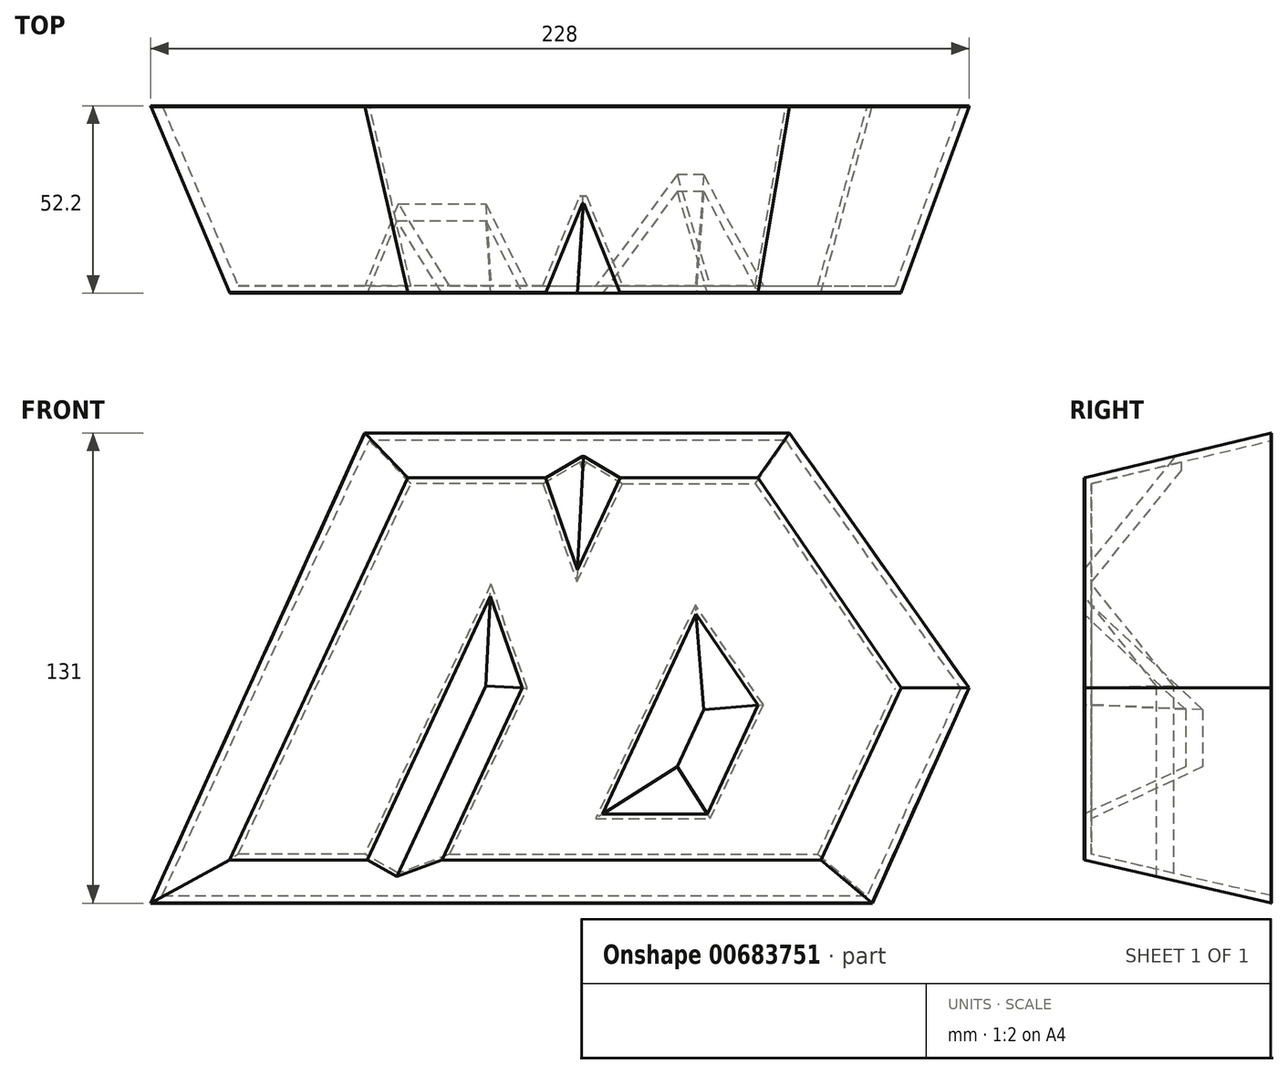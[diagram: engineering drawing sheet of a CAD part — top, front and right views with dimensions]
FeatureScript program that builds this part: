
annotation { "Feature Type Name" : "Feature", "Feature Type Description" : "" }
export const myFeature = defineFeature(function(context is Context, id is Id, definition is map)
    precondition{}
    {
        {
            var Q0;
            Q0=qCreatedBy(makeId("Front.planeOp"),FACE);
            var sketch = newSketch(context, id + "F0", { "sketchPlane" : qUnion([Q0])});
            skLineSegment(sketch, "E0", {"start": v(0, 0) * mm, "end": v(38.4, 0) * mm});
            skLineSegment(sketch, "E1", {"start": v(38.4, 0) * mm, "end": v(72.72, 73.6) * mm});
            skLineSegment(sketch, "E2", {"start": v(72.72, 73.6) * mm, "end": v(81.58, 48) * mm});
            skLineSegment(sketch, "E3", {"start": v(81.58, 48) * mm, "end": v(59.2, 0) * mm});
            skLineSegment(sketch, "E4", {"start": v(59.2, 0) * mm, "end": v(164.8, 0) * mm});
            skLineSegment(sketch, "E5", {"start": v(164.8, 0) * mm, "end": v(187.18, 48) * mm});
            skLineSegment(sketch, "E6", {"start": v(187.18, 48) * mm, "end": v(147.29, 106.56) * mm});
            skLineSegment(sketch, "E7", {"start": v(147.29, 106.56) * mm, "end": v(108.89, 106.56) * mm});
            skLineSegment(sketch, "E8", {"start": v(108.89, 106.56) * mm, "end": v(96.95, 80.96) * mm});
            skLineSegment(sketch, "E9", {"start": v(96.95, 80.96) * mm, "end": v(88.09, 106.56) * mm});
            skLineSegment(sketch, "E10", {"start": v(88.09, 106.56) * mm, "end": v(49.69, 106.56) * mm});
            skLineSegment(sketch, "E11", {"start": v(49.69, 106.56) * mm, "end": v(0, 0) * mm});
            skLineSegment(sketch, "E12", {"start": v(104, 12.8) * mm, "end": v(133.12, 12.8) * mm});
            skLineSegment(sketch, "E13", {"start": v(133.12, 12.8) * mm, "end": v(147.29, 43.19) * mm});
            skLineSegment(sketch, "E14", {"start": v(147.29, 43.19) * mm, "end": v(130, 68.56) * mm});
            skLineSegment(sketch, "E15", {"start": v(130, 68.56) * mm, "end": v(104, 12.8) * mm});
            skLineSegment(sketch, "E16", {"start": v(38.4, 0) * mm, "end": v(59.2, 0) * mm});
            skLineSegment(sketch, "E17", {"start": v(88.09, 106.56) * mm, "end": v(108.89, 106.56) * mm});
            skSolve(sketch);
        }
        {
            var Q0;
            Q0=qCreatedBy(makeId("Front.planeOp"),FACE);
            cPlane(context, id + "F1", {"entities" : qUnion([Q0]), "cplaneType" : CPlaneType.OFFSET, "offset" : 52 * mm, "oppositeDirection" : true, "width" : 150 * mm, "height" : 150 * mm});
        }
        {
            var Q0;
            Q0=qCreatedBy(id+"F1.planeOp",FACE);
            var sketch = newSketch(context, id + "F2", { "sketchPlane" : qUnion([Q0])});
            skLineSegment(sketch, "E18", {"start": v(179.07, -12) * mm, "end": v(206.07, 48) * mm});
            skLineSegment(sketch, "E19", {"start": v(206.07, 48) * mm, "end": v(156.07, 119) * mm});
            skLineSegment(sketch, "E20", {"start": v(37.7, 119) * mm, "end": v(-21.93, -12) * mm});
            skLineSegment(sketch, "E21", {"start": v(-21.93, -12) * mm, "end": v(179.07, -12) * mm});
            skLineSegment(sketch, "E22", {"start": v(37.69, 119) * mm, "end": v(156.07, 119) * mm});
            skSolve(sketch);
        }
        {
            var Q0;
            Q0=makeQuery(id+"F0.imprint","IMPRINT",FACE,{"disambiguationData":[TD([[makeQuery(id+"F0.imprint","IMPRINT",EDGE,{"derivedFrom":sQuery(id+"F0.wireOp",EDGE,"E12")}),1.0]])]});
            var Q1;
            Q1=makeQuery(id+"F2.imprint","IMPRINT",FACE,{"disambiguationData":[TD([[makeQuery(id+"F2.imprint","IMPRINT",EDGE,{"derivedFrom":sQuery(id+"F2.wireOp",EDGE,"92f5ff60-c0ba-45f9-92b4-fe02d9dd4104")}),1.0]])]});
            var Q2;
            Q2=makeQuery(id+"F2.imprint","IMPRINT",FACE,{"disambiguationData":[TD([[makeQuery(id+"F2.imprint","IMPRINT",EDGE,{"derivedFrom":sQuery(id+"F2.wireOp",EDGE,"39e3cdb1-03fe-4b67-bd12-042c1df5d7d2")}),1.0]])]});
            var Q3;
            Q3=makeQuery(id+"F0.imprint","IMPRINT",FACE,{"disambiguationData":[TD([[makeQuery(id+"F0.imprint","IMPRINT",EDGE,{"derivedFrom":sQuery(id+"F0.wireOp",EDGE,"E0")}),1.0]])]});
            var Q4;
            Q4=makeQuery(id+"F0.imprint","IMPRINT",FACE,{"disambiguationData":[TD([[makeQuery(id+"F0.imprint","IMPRINT",EDGE,{"derivedFrom":sQuery(id+"F0.wireOp",EDGE,"E8")}),-1.0]])]});
            var Q5;
            Q5=makeQuery(id+"F0.imprint","IMPRINT",FACE,{"disambiguationData":[TD([[makeQuery(id+"F0.imprint","IMPRINT",EDGE,{"derivedFrom":sQuery(id+"F0.wireOp",EDGE,"E1")}),-1.0]])]});
            var Q6;
            Q6=makeQuery(id+"F2.imprint","IMPRINT",FACE,{"disambiguationData":[TD([[makeQuery(id+"F2.imprint","IMPRINT",EDGE,{"derivedFrom":sQuery(id+"F2.wireOp",EDGE,"E18")}),1.0]])]});
            extrude(context, id + "F3", {"entities" : qUnion([Q0, Q1, Q2, Q3, Q4, Q5, Q6]), "oppositeDirection" : true, "depth" : 0.2 * mm, "offsetDistance" : 25 * mm});
        }
        {
            var Q2;
            Q2=makeQuery(id+"F3.opExtrude","CAP_FACE",FACE,{"disambiguationData":[OSD([sQuery(id+"F0.wireOp",EDGE,"E0"),sQuery(id+"F0.wireOp",EDGE,"E1"),sQuery(id+"F0.wireOp",EDGE,"E2"),sQuery(id+"F0.wireOp",EDGE,"E3"),sQuery(id+"F0.wireOp",EDGE,"E4"),sQuery(id+"F0.wireOp",EDGE,"E5"),sQuery(id+"F0.wireOp",EDGE,"E6"),sQuery(id+"F0.wireOp",EDGE,"E7"),sQuery(id+"F0.wireOp",EDGE,"E8"),sQuery(id+"F0.wireOp",EDGE,"E9"),sQuery(id+"F0.wireOp",EDGE,"E10"),sQuery(id+"F0.wireOp",EDGE,"E11")])],"isStart":false});
            var Q3;
            Q3=makeQuery(id+"F3.opExtrude","CAP_FACE",FACE,{"disambiguationData":[OSD([sQuery(id+"F2.wireOp",EDGE,"39e3cdb1-03fe-4b67-bd12-042c1df5d7d2"),sQuery(id+"F2.wireOp",EDGE,"b41d93aa-d4e3-4370-a6f8-97417ad040d7"),sQuery(id+"F2.wireOp",EDGE,"948f9560-f6c3-429f-b71c-48599e3f52fe"),sQuery(id+"F2.wireOp",EDGE,"983bbde8-c430-40ac-8f2e-028eaffca171"),sQuery(id+"F2.wireOp",EDGE,"f54a0fac-325c-4034-9938-b5489e34c121"),sQuery(id+"F2.wireOp",EDGE,"E18"),sQuery(id+"F2.wireOp",EDGE,"E19"),sQuery(id+"F2.wireOp",EDGE,"f148eaec-45fb-4050-9e8e-855f834db8f8"),sQuery(id+"F2.wireOp",EDGE,"3d92075d-585f-46b2-b87d-c5ed2a65604b"),sQuery(id+"F2.wireOp",EDGE,"620fad5a-e794-4931-833f-fb92f4ff3776"),sQuery(id+"F2.wireOp",EDGE,"3ae3cf3c-2123-4031-be0f-effaeb8d2633"),sQuery(id+"F2.wireOp",EDGE,"E20")])],"isStart":false});
            loft(context, id + "F4", {"operationType" : NewBodyOperationType.ADD, "sheetProfilesArray" : [{ "sheetProfileEntities" : qUnion([Q2]) }, { "sheetProfileEntities" : qUnion([Q3]) }]});
        }
        {
            var Q0;
            Q0=makeQuery(id+"F0.imprint","IMPRINT",FACE,{"disambiguationData":[TD([[makeQuery(id+"F0.imprint","IMPRINT",EDGE,{"derivedFrom":sQuery(id+"F0.wireOp",EDGE,"E12")}),1.0]])]});
            extrude(context, id + "F5", {"entities" : qUnion([Q0]), "operationType" : NewBodyOperationType.REMOVE, "oppositeDirection" : true, "depth" : 30 * mm, "offsetDistance" : 25 * mm, "hasDraft" : true, "draftAngle" : 25 * degree, "draftPullDirection" : true});
        }
        {
            var Q0;
            Q0=makeQuery(id+"F0.imprint","IMPRINT",FACE,{"disambiguationData":[TD([[makeQuery(id+"F0.imprint","IMPRINT",EDGE,{"derivedFrom":sQuery(id+"F0.wireOp",EDGE,"E0")}),1.0]])]});
            var sketch = newSketch(context, id + "F6", { "sketchPlane" : qUnion([Q0])});
            skLineSegment(sketch, "E23", {"start": v(96.95, 80.96) * mm, "end": v(66, 170.39) * mm});
            skLineSegment(sketch, "E24", {"start": v(66, 170.39) * mm, "end": v(138.65, 170.39) * mm});
            skLineSegment(sketch, "E25", {"start": v(138.65, 170.39) * mm, "end": v(96.95, 80.96) * mm});
            skLineSegment(sketch, "E26", {"start": v(72.72, 73.6) * mm, "end": v(81.58, 48) * mm});
            skLineSegment(sketch, "E27", {"start": v(81.58, 48) * mm, "end": v(46.4, -27.45) * mm});
            skLineSegment(sketch, "E28", {"start": v(46.4, -27.45) * mm, "end": v(25.6, -27.45) * mm});
            skLineSegment(sketch, "E29", {"start": v(25.6, -27.45) * mm, "end": v(72.72, 73.6) * mm});
            skSolve(sketch);
        }
        {
            var Q0;
            {var subQ2=sQuery(id+"F6.wireOp",EDGE,"E24");Q0=makeQuery(id+"F6.imprint","IMPRINT",FACE,{"disambiguationData":[TD([[makeQuery(id+"F6.imprint","IMPRINT",EDGE,{"derivedFrom":subQ2}),-1.0]])]});}
            var Q1;
            {var subQ3=sQuery(id+"F6.wireOp",EDGE,"E26");Q1=makeQuery(id+"F6.imprint","IMPRINT",FACE,{"disambiguationData":[TD([[makeQuery(id+"F6.imprint","IMPRINT",EDGE,{"derivedFrom":subQ3}),-1.0]])]});}
            extrude(context, id + "F7", {"entities" : qUnion([Q0, Q1]), "operationType" : NewBodyOperationType.REMOVE, "oppositeDirection" : true, "depth" : 25 * mm, "offsetDistance" : 25 * mm, "hasDraft" : true, "draftAngle" : 25 * degree, "draftPullDirection" : true});
        }
        {
            var Q0;
            Q0=makeQuery(id+"F3.opExtrude","CAP_FACE",FACE,{"disambiguationData":[OSD([sQuery(id+"F2.wireOp",EDGE,"39e3cdb1-03fe-4b67-bd12-042c1df5d7d2"),sQuery(id+"F2.wireOp",EDGE,"f54a0fac-325c-4034-9938-b5489e34c121"),sQuery(id+"F2.wireOp",EDGE,"E18"),sQuery(id+"F2.wireOp",EDGE,"E19"),sQuery(id+"F2.wireOp",EDGE,"f148eaec-45fb-4050-9e8e-855f834db8f8"),sQuery(id+"F2.wireOp",EDGE,"3ae3cf3c-2123-4031-be0f-effaeb8d2633"),sQuery(id+"F2.wireOp",EDGE,"E20"),sQuery(id+"F2.wireOp",EDGE,"rUrhFJFD-ZHFD-4oyR-CUCE-ujCQtW2GheMh"),sQuery(id+"F2.wireOp",EDGE,"FnvXKyAz-NL8B-mhme-6fHg-3dOLzGpfnLAi")])],"isStart":false});
            shell(context, id + "F8", {"entities" : qUnion([Q0]), "thickness" : 2 * mm});
        }
        {
            var Q0;
            Q0=qCreatedBy(makeId("Top.planeOp"),FACE);
            cPlane(context, id + "F9", {"entities" : qUnion([Q0]), "cplaneType" : CPlaneType.OFFSET, "offset" : 145 * mm, "width" : 150 * mm, "height" : 150 * mm});
        }
    });
